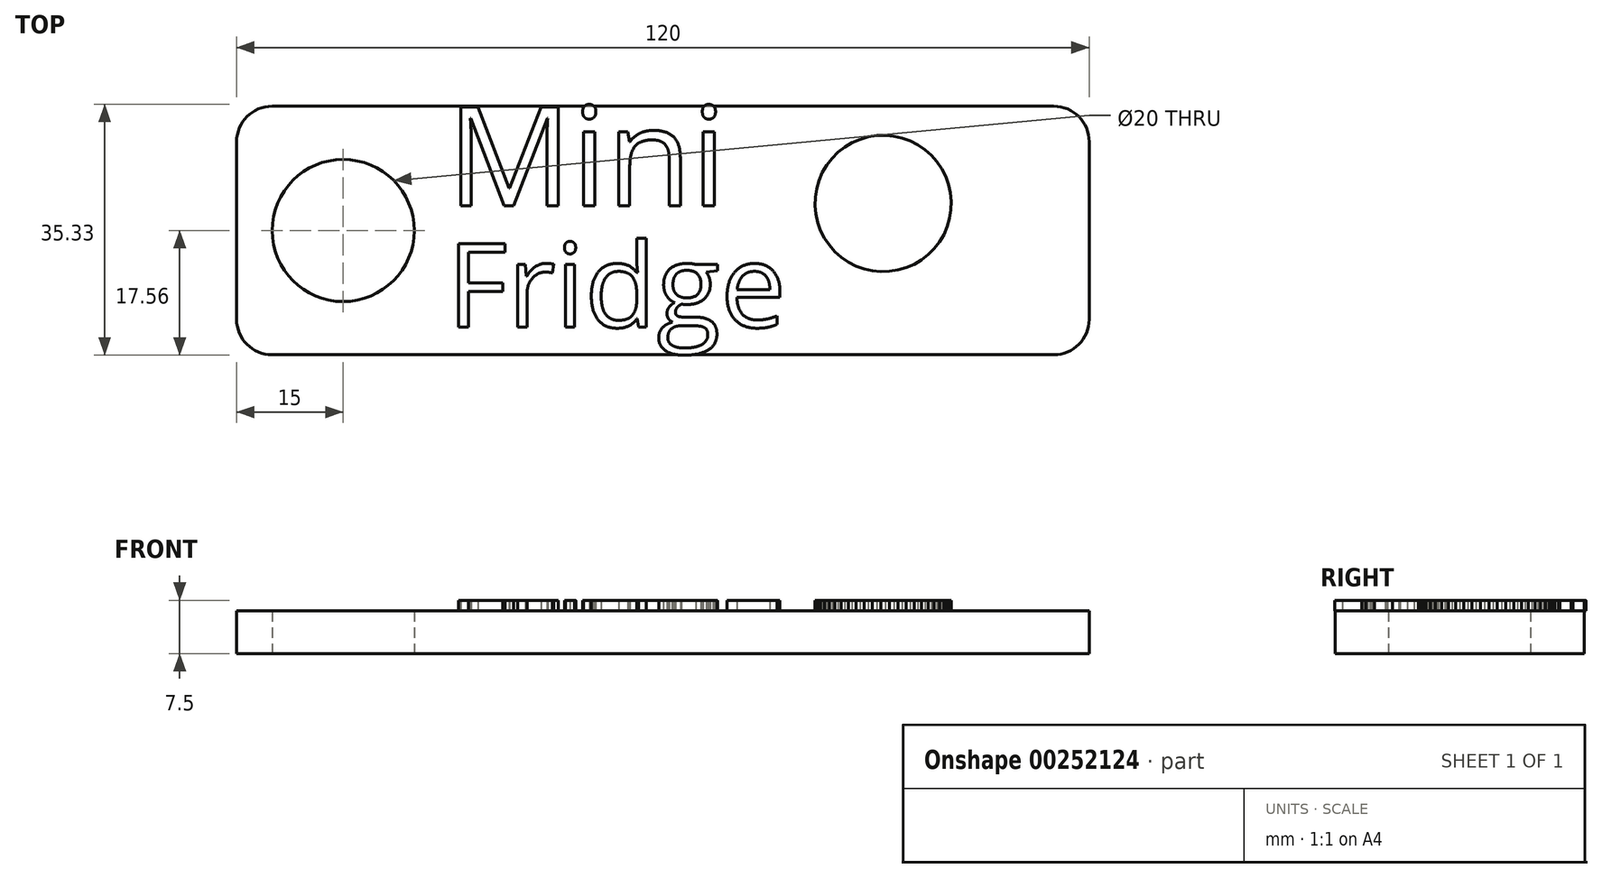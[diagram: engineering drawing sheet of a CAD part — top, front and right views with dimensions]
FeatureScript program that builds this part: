
annotation { "Feature Type Name" : "Feature", "Feature Type Description" : "" }
export const myFeature = defineFeature(function(context is Context, id is Id, definition is map)
    precondition{}
    {
        {
            var Q0;
            Q0=qCreatedBy(makeId("Top.planeOp"),FACE);
            var sketch = newSketch(context, id + "F0", { "sketchPlane" : qUnion([Q0])});
            skLineSegment(sketch, "E0.bottom", {"start": v(-60, 17.5) * mm, "end": v(60, 17.5) * mm});
            skLineSegment(sketch, "E0.top", {"start": v(-60, -17.5) * mm, "end": v(60, -17.5) * mm});
            skLineSegment(sketch, "E0.left", {"start": v(-60, 17.5) * mm, "end": v(-60, -17.5) * mm});
            skLineSegment(sketch, "E0.right", {"start": v(60, 17.5) * mm, "end": v(60, -17.5) * mm});
            skPoint(sketch, "E0.middle", {"position": v(0, 0) * mm});
            skCircle(sketch, "E1", {"center": v(-45, 0) * mm, "radius": 10 * mm});
            skSolve(sketch);
        }
        {
            var Q0;
            Q0=makeQuery(id+"F0.imprint","IMPRINT",FACE,{"disambiguationData":[TD([[makeQuery(id+"F0.imprint","IMPRINT",EDGE,{"derivedFrom":sQuery(id+"F0.wireOp",EDGE,"E0.bottom")}),-1.0]])]});
            extrude(context, id + "F1", {"entities" : qUnion([Q0]), "depth" : 6 * mm});
        }
        {
            var Q0;
            Q0=makeQuery(id+"F1.opExtrude","SWEPT_EDGE",EDGE,{"disambiguationData":[OSD([sQuery(id+"F0.wireOp",EDGE,"E0.top"),sQuery(id+"F0.wireOp",EDGE,"E0.right")])]});
            var Q1;
            Q1=makeQuery(id+"F1.opExtrude","SWEPT_EDGE",EDGE,{"disambiguationData":[OSD([sQuery(id+"F0.wireOp",EDGE,"E0.bottom"),sQuery(id+"F0.wireOp",EDGE,"E0.right")])]});
            var Q2;
            Q2=makeQuery(id+"F1.opExtrude","SWEPT_EDGE",EDGE,{"disambiguationData":[OSD([sQuery(id+"F0.wireOp",EDGE,"E0.top"),sQuery(id+"F0.wireOp",EDGE,"E0.left")])]});
            var Q3;
            Q3=makeQuery(id+"F1.opExtrude","SWEPT_EDGE",EDGE,{"disambiguationData":[OSD([sQuery(id+"F0.wireOp",EDGE,"E0.bottom"),sQuery(id+"F0.wireOp",EDGE,"E0.left")])]});
            fillet(context, id + "F2", {"entities" : qUnion([Q0, Q1, Q2, Q3]), "radius" : 5 * mm, "tangentPropagation" : true, "allowEdgeOverflow" : false});
        }
        {
            var Q0;
            Q0=makeQuery(id+"F1.opExtrude","CAP_FACE",FACE,{"disambiguationData":[OSD([sQuery(id+"F0.wireOp",EDGE,"E0.bottom"),sQuery(id+"F0.wireOp",EDGE,"E0.top"),sQuery(id+"F0.wireOp",EDGE,"E0.left"),sQuery(id+"F0.wireOp",EDGE,"E0.right"),sQuery(id+"F0.wireOp",EDGE,"E1")])],"isStart":false});
            var sketch = newSketch(context, id + "F3", { "sketchPlane" : qUnion([Q0])});
            skLineSegment(sketch, "E2", {"start": v(-30.37, 12.5) * mm, "end": v(-30.37, -16.01) * mm, "construction": true});
            skText(sketch, "E3", { "text": "Mini", "fontName": "OpenSans-Regular.ttf"});
            skText(sketch, "E4", { "text": "Fridge", "fontName": "OpenSans-Regular.ttf"});
            skCircle(sketch, "E5.cCircle", {"center": v(31, 3.8) * mm, "radius": 9.58 * mm, "construction": true});
            skLineSegment(sketch, "E5.0", {"start": v(40.02, 0.55) * mm, "end": v(39.54, -0.55) * mm});
            skLineSegment(sketch, "E5.1", {"start": v(39.54, -0.55) * mm, "end": v(38.93, -1.6) * mm});
            skLineSegment(sketch, "E5.2", {"start": v(38.93, -1.6) * mm, "end": v(38.19, -2.54) * mm});
            skLineSegment(sketch, "E5.3", {"start": v(38.19, -2.54) * mm, "end": v(37.34, -3.4) * mm});
            skLineSegment(sketch, "E5.4", {"start": v(37.34, -3.4) * mm, "end": v(36.38, -4.13) * mm});
            skLineSegment(sketch, "E5.5", {"start": v(36.38, -4.13) * mm, "end": v(35.35, -4.75) * mm});
            skLineSegment(sketch, "E5.6", {"start": v(35.35, -4.75) * mm, "end": v(34.24, -5.22) * mm});
            skLineSegment(sketch, "E5.7", {"start": v(34.24, -5.22) * mm, "end": v(33.08, -5.56) * mm});
            skLineSegment(sketch, "E5.8", {"start": v(33.08, -5.56) * mm, "end": v(31.9, -5.75) * mm});
            skLineSegment(sketch, "E5.9", {"start": v(31.9, -5.75) * mm, "end": v(30.69, -5.79) * mm});
            skLineSegment(sketch, "E5.10", {"start": v(30.69, -5.79) * mm, "end": v(29.49, -5.67) * mm});
            skLineSegment(sketch, "E5.11", {"start": v(29.49, -5.67) * mm, "end": v(28.31, -5.4) * mm});
            skLineSegment(sketch, "E5.12", {"start": v(28.31, -5.4) * mm, "end": v(27.18, -5) * mm});
            skLineSegment(sketch, "E5.13", {"start": v(27.18, -5) * mm, "end": v(26.1, -4.45) * mm});
            skLineSegment(sketch, "E5.14", {"start": v(26.1, -4.45) * mm, "end": v(25.1, -3.77) * mm});
            skLineSegment(sketch, "E5.15", {"start": v(25.1, -3.77) * mm, "end": v(24.2, -2.98) * mm});
            skLineSegment(sketch, "E5.16", {"start": v(24.2, -2.98) * mm, "end": v(23.4, -2.07) * mm});
            skLineSegment(sketch, "E5.17", {"start": v(23.4, -2.07) * mm, "end": v(22.73, -1.08) * mm});
            skLineSegment(sketch, "E5.18", {"start": v(22.73, -1.08) * mm, "end": v(22.18, 0) * mm});
            skLineSegment(sketch, "E5.19", {"start": v(22.18, 0) * mm, "end": v(21.78, 1.13) * mm});
            skLineSegment(sketch, "E5.20", {"start": v(21.78, 1.13) * mm, "end": v(21.51, 2.3) * mm});
            skLineSegment(sketch, "E5.21", {"start": v(21.51, 2.3) * mm, "end": v(21.4, 3.5) * mm});
            skLineSegment(sketch, "E5.22", {"start": v(21.4, 3.5) * mm, "end": v(21.44, 4.71) * mm});
            skLineSegment(sketch, "E5.23", {"start": v(21.44, 4.71) * mm, "end": v(21.63, 5.9) * mm});
            skLineSegment(sketch, "E5.24", {"start": v(21.63, 5.9) * mm, "end": v(21.96, 7.06) * mm});
            skLineSegment(sketch, "E5.25", {"start": v(21.96, 7.06) * mm, "end": v(22.44, 8.17) * mm});
            skLineSegment(sketch, "E5.26", {"start": v(22.44, 8.17) * mm, "end": v(23.06, 9.2) * mm});
            skLineSegment(sketch, "E5.27", {"start": v(23.06, 9.2) * mm, "end": v(23.8, 10.16) * mm});
            skLineSegment(sketch, "E5.28", {"start": v(23.8, 10.16) * mm, "end": v(24.65, 11) * mm});
            skLineSegment(sketch, "E5.29", {"start": v(24.65, 11) * mm, "end": v(25.6, 11.75) * mm});
            skLineSegment(sketch, "E5.30", {"start": v(25.6, 11.75) * mm, "end": v(26.64, 12.36) * mm});
            skLineSegment(sketch, "E5.31", {"start": v(26.64, 12.36) * mm, "end": v(27.75, 12.84) * mm});
            skLineSegment(sketch, "E5.32", {"start": v(27.75, 12.84) * mm, "end": v(28.9, 13.17) * mm});
            skLineSegment(sketch, "E5.33", {"start": v(28.9, 13.17) * mm, "end": v(30.1, 13.36) * mm});
            skLineSegment(sketch, "E5.34", {"start": v(30.1, 13.36) * mm, "end": v(31.3, 13.4) * mm});
            skLineSegment(sketch, "E5.35", {"start": v(31.3, 13.4) * mm, "end": v(32.5, 13.29) * mm});
            skLineSegment(sketch, "E5.36", {"start": v(32.5, 13.29) * mm, "end": v(33.67, 13.02) * mm});
            skLineSegment(sketch, "E5.37", {"start": v(33.67, 13.02) * mm, "end": v(34.8, 12.61) * mm});
            skLineSegment(sketch, "E5.38", {"start": v(34.8, 12.61) * mm, "end": v(35.88, 12.07) * mm});
            skLineSegment(sketch, "E5.39", {"start": v(35.88, 12.07) * mm, "end": v(36.88, 11.39) * mm});
            skLineSegment(sketch, "E5.40", {"start": v(36.88, 11.39) * mm, "end": v(37.78, 10.6) * mm});
            skLineSegment(sketch, "E5.41", {"start": v(37.78, 10.6) * mm, "end": v(38.58, 9.69) * mm});
            skLineSegment(sketch, "E5.42", {"start": v(38.58, 9.69) * mm, "end": v(39.26, 8.69) * mm});
            skLineSegment(sketch, "E5.43", {"start": v(39.26, 8.69) * mm, "end": v(39.8, 7.62) * mm});
            skLineSegment(sketch, "E5.44", {"start": v(39.8, 7.62) * mm, "end": v(40.21, 6.48) * mm});
            skLineSegment(sketch, "E5.45", {"start": v(40.21, 6.48) * mm, "end": v(40.47, 5.3) * mm});
            skLineSegment(sketch, "E5.46", {"start": v(40.47, 5.3) * mm, "end": v(40.59, 4.1) * mm});
            skLineSegment(sketch, "E5.47", {"start": v(40.59, 4.1) * mm, "end": v(40.55, 2.9) * mm});
            skLineSegment(sketch, "E5.48", {"start": v(40.55, 2.9) * mm, "end": v(40.36, 1.71) * mm});
            skLineSegment(sketch, "E5.49", {"start": v(40.36, 1.71) * mm, "end": v(40.02, 0.55) * mm});
            skPoint(sketch, "E5.0.midPoint", {"position": v(39.78, 0) * mm});
            const initialGuessF3  = {"E3": [-0.03037, 0.00351, 1, 0, 0.01399], "E4": [-0.03037, -0.0136, 1, 0, 0.01185]};
            skSetInitialGuess(sketch, initialGuessF3);
            skSolve(sketch);
        }
        {
            var Q0;
            Q0 = qSketchRegion(id + "F3", true);
            extrude(context, id + "F4", {"entities" : qUnion([Q0]), "operationType" : NewBodyOperationType.ADD, "depth" : 1.5 * mm});
        }
    });
